# Revit family: 51162180
name_source: partatom
category: Plumbing Fixtures
units: mm (PartAtom-declared; Revit-internal decimal feet)

## family parameters
Always vertical = Yes
Cut with Voids When Loaded = No
OmniClass Number = 23.45.55.00
OmniClass Title = Sanitary Faucets, Wastes
Part Type = Normal
Room Calculation Point = No
Round Connector Dimension = Use Diameter
Shared = No
Work Plane-Based = No

## types (1)
- 51162180 Spout
    2D/3D/BIM Files URL = http://static.hansa.com
    3D View = https://static.hansa.com
    Advanced Features = Inner body made of DZR brass
    Aerator = Hidden aerator;Laminar stream
    Ambience photo = http://static.hansa.com
    AssetType = Fixed
    BIMObjectName = 51162180
    BodyMaterial = Brass
    Brand = HANSA
    Catalog Drawing URL = http://static.hansa.com
    Category = Bathtub & Shower
    CloseOffRating = 0
    Color = Chrome
    Concealed Parts = Square rosette;Round rosette;Soft edge rosette
    Connection Size = G1/2
    DN Size = 24.5 mm
    Default Elevation = 0 mm  [stored 0 ft]
    Dimension Drawing URL = http://static.hansa.com
    DurationUnit = Year
    EAN Number = 4057304006975
    EN Standard = EN 817
    ETIM Class Number = EC011421 Outlet for sanitary taps
    FDV Document URL = http://www.hansa.com
    FaucetMainMaterial = Brass
    Finish = Polished
    Flow Drawing URL = http://static.hansa.com
    Flow Rate At 300kPa = 0.0 L/s
    FlowCoefficient = 0
    Group = Spout
    IfcExportAs = IfcValveType
    IfcExportType = FAUCET
    Installation Type = Wall mounted
    Installation and Maintenance Guide URL = http://static.hansa.com
    Interactive AR View URL = https://static.hansa.com
    Manufacturer = HANSA
    ManufacturerName = HANSA
    ManufacturerURL = http://www.hansa.com
    Market = International;Germany;Austria;Belgium;Netherlands;France;Czech Republic;Slovakia;Spain
    Material = Brass
    Max. Hot Water Supply = 80 °C
    Mobile Product Information URL = http://mpi.hansa.com
    Model = 51162180 Spout
    ModelReference = 51162180
    NBSDescription = Water supply fittings for wash basins and troughs
    NBSReference = 45-35-70/371
    Name = 51162180 Spout
    Name_en = 51162180 Spout
    NominalDepth = 212 mm  [stored 0.695538 ft]
    NominalDiameter = 25 mm  [stored 0.082021 ft]
    NominalHeight = 75 mm  [stored 0.246063 ft]
    NominalLength = 212 mm  [stored 0.695538 ft]
    NominalWidth = 75 mm  [stored 0.246063 ft]
    Product Code = 51162180
    Product Family = HANSADESIGNO
    Product Image URL = http://static.hansa.com
    Product URL = http://static.hansa.com
    Sales Package dimensions (LxWxH) = 210 x 165 x 60
    Shape = Sculptured
    Size = 75x212x109 mm
    Spout Projection = 195 mm
    Spout Type = Fixed spout;Casted construction
    Surface treatment = Chrome
    Technical DataSheet URL = http://www.hansa.com
    UNSPSC Class Number = 30181807 Spout
    URL Declaration Of Performance (DOP) = http://static.hansa.com
    URL Declaration of Asbestos = http://static.hansa.com
    URL Declaration of Conformity = http://static.hansa.com
    URL Declaration of SCIP = http://static.hansa.com
    URL EU Packaging Declaration = http://static.hansa.com
    URL EcoLabel Declaration = http://static.hansa.com
    URL REACH = http://static.hansa.com
    Uniclass2 = Pr_40_30_96_97
    Uniclass2015Description = Washbasin spouts
    Uniclass2015Reference = Pr_40_20_87_97
    Version = 1
    VersionDate = 01/06/2023
    Warranty Information URL = http://warranty.hansa.com
    WarrantyDescription = http://warranty.hansa.com
    WarrantyDurationUnit = Year
    Working Pressure = 50 - 1000 kPa

note: [stored X ft] marks values corroborated as IEEE doubles in the binary element streams (Revit-internal decimal feet)

## geometry (parser evidence)
native form markers: Sweep x5
no freeform markers — native parametric forms only
